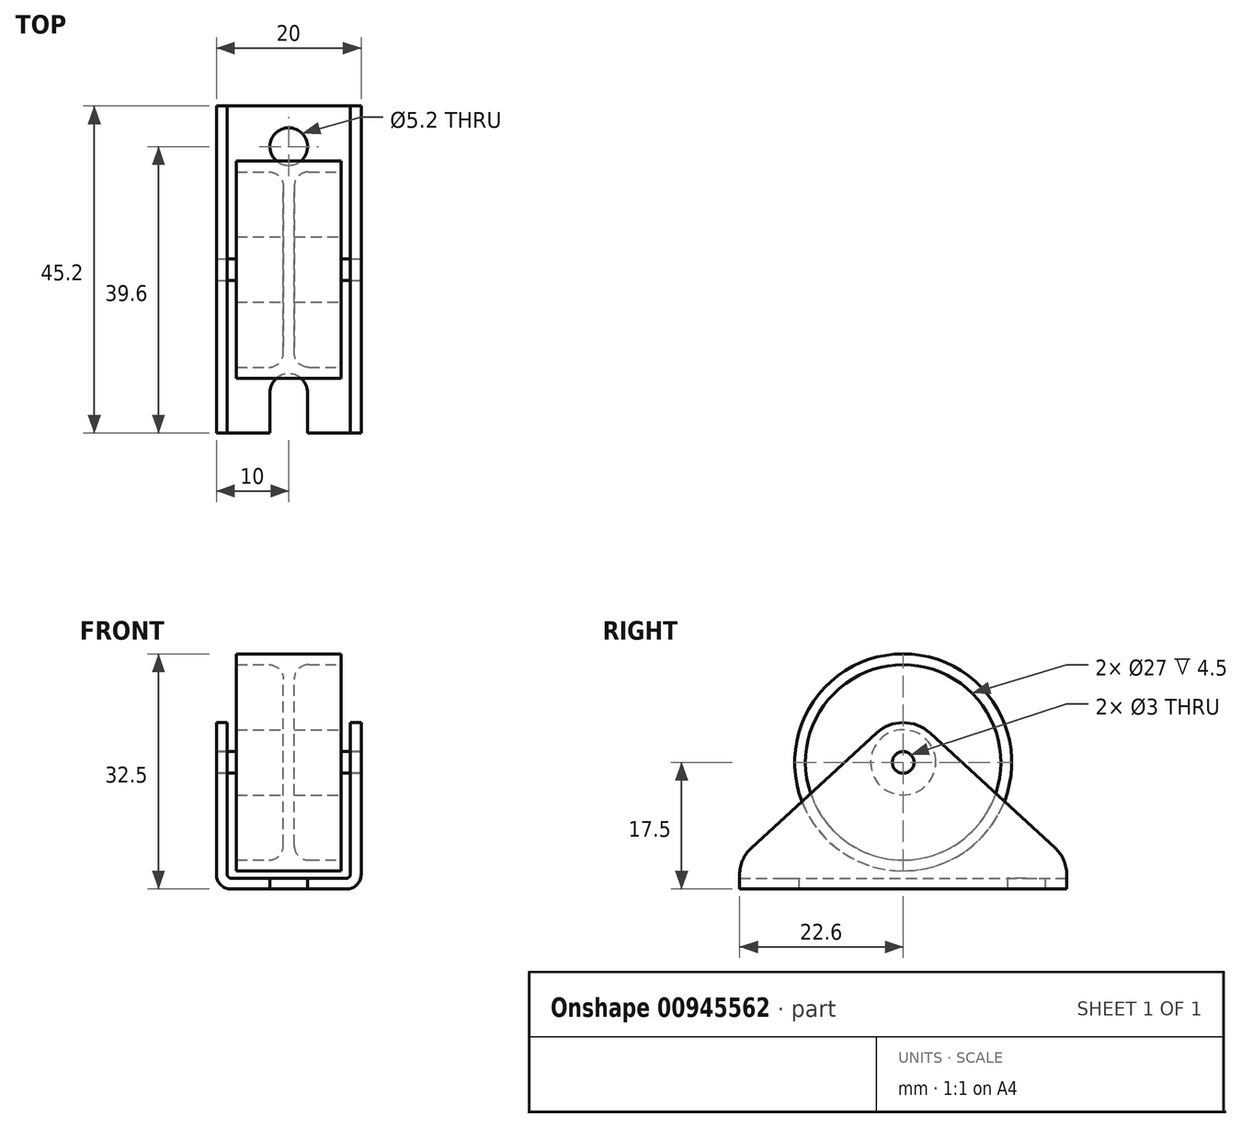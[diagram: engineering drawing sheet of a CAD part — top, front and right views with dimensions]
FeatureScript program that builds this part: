
annotation { "Feature Type Name" : "Feature", "Feature Type Description" : "" }
export const myFeature = defineFeature(function(context is Context, id is Id, definition is map)
    precondition{}
    {
        {
            var Q0;
            Q0=qCreatedBy(makeId("Front.planeOp"),FACE);
            var sketch = newSketch(context, id + "F0", { "sketchPlane" : qUnion([Q0])});
            skLineSegment(sketch, "E0.bottom", {"start": v(-8, 0) * mm, "end": v(8, 0) * mm});
            skLineSegment(sketch, "E0.top", {"start": v(-10, 23) * mm, "end": v(-8.5, 23) * mm});
            skLineSegment(sketch, "E0.left", {"start": v(-10, 2) * mm, "end": v(-10, 23) * mm});
            skLineSegment(sketch, "E0.right", {"start": v(10, 2) * mm, "end": v(10, 23) * mm});
            skLineSegment(sketch, "E1.0", {"start": v(-8.5, 2) * mm, "end": v(-8.5, 23) * mm});
            skLineSegment(sketch, "E1.1", {"start": v(-8, 1.5) * mm, "end": v(8, 1.5) * mm});
            skLineSegment(sketch, "E1.2", {"start": v(8.5, 2) * mm, "end": v(8.5, 23) * mm});
            skPoint(sketch, "E2.visualSharp", {"position": v(-8.5, 1.5) * mm});
            skArc(sketch, "E2.filletArc", {"start": v(-8.5, 2) * mm, "mid": v(-8.35, 1.65) * mm, "end": v(-8, 1.5) * mm});
            skLineSegment(sketch, "E3", {"start": v(8.5, 23) * mm, "end": v(10, 23) * mm});
            skPoint(sketch, "E4.visualSharp", {"position": v(8.5, 1.5) * mm});
            skArc(sketch, "E4.filletArc", {"start": v(8, 1.5) * mm, "mid": v(8.35, 1.65) * mm, "end": v(8.5, 2) * mm});
            skPoint(sketch, "E5.visualSharp", {"position": v(-10, 0) * mm});
            skArc(sketch, "E5.filletArc", {"start": v(-10, 2) * mm, "mid": v(-9.41, 0.59) * mm, "end": v(-8, 0) * mm});
            skPoint(sketch, "E6.visualSharp", {"position": v(10, 0) * mm});
            skArc(sketch, "E6.filletArc", {"start": v(8, 0) * mm, "mid": v(9.41, 0.59) * mm, "end": v(10, 2) * mm});
            skPoint(sketch, "E7", {"position": v(0, 0) * mm});
            skLineSegment(sketch, "E8", {"start": v(0, 0) * mm, "end": v(0, 28.77) * mm, "construction": true});
            skLineSegment(sketch, "E9", {"start": v(0, 32.5) * mm, "end": v(7.25, 32.5) * mm});
            skLineSegment(sketch, "E10", {"start": v(7.25, 32.5) * mm, "end": v(7.25, 31) * mm});
            skLineSegment(sketch, "E11", {"start": v(7.25, 31) * mm, "end": v(2.75, 31) * mm});
            skLineSegment(sketch, "E12", {"start": v(0.75, 29) * mm, "end": v(0.75, 22) * mm});
            skLineSegment(sketch, "E13", {"start": v(0.75, 22) * mm, "end": v(7.25, 22) * mm});
            skLineSegment(sketch, "E14", {"start": v(7.25, 22) * mm, "end": v(7.25, 19) * mm});
            skLineSegment(sketch, "E15", {"start": v(7.25, 19) * mm, "end": v(8.5, 19) * mm});
            skLineSegment(sketch, "E16", {"start": v(8.5, 17.5) * mm, "end": v(0, 17.5) * mm});
            skPoint(sketch, "E17.visualSharp", {"position": v(0.75, 31) * mm});
            skArc(sketch, "E17.filletArc", {"start": v(2.75, 31) * mm, "mid": v(1.34, 30.41) * mm, "end": v(0.75, 29) * mm});
            skLineSegment(sketch, "E18", {"start": v(7.25, 22) * mm, "end": v(7.25, 31) * mm, "construction": true});
            skLineSegment(sketch, "E19.0.MirrorCS", {"start": v(-8.5, 17.5) * mm, "end": v(0, 17.5) * mm});
            skLineSegment(sketch, "E20.0.MirrorCS", {"start": v(-7.25, 19) * mm, "end": v(-8.5, 19) * mm});
            skLineSegment(sketch, "E21.0.MirrorCS", {"start": v(-7.25, 22) * mm, "end": v(-7.25, 19) * mm});
            skLineSegment(sketch, "E22.0.MirrorCS", {"start": v(-0.75, 22) * mm, "end": v(-7.25, 22) * mm});
            skLineSegment(sketch, "E23.0.MirrorCS", {"start": v(-0.75, 29) * mm, "end": v(-0.75, 22) * mm});
            skArc(sketch, "E24.0.MirrorCS", {"start": v(-2.75, 31) * mm, "mid": v(-1.34, 30.41) * mm, "end": v(-0.75, 29) * mm});
            skLineSegment(sketch, "E25.0.MirrorCS", {"start": v(-7.25, 31) * mm, "end": v(-2.75, 31) * mm});
            skLineSegment(sketch, "E26.0.MirrorCS", {"start": v(-7.25, 32.5) * mm, "end": v(-7.25, 31) * mm});
            skLineSegment(sketch, "E27.0.MirrorCS", {"start": v(0, 32.5) * mm, "end": v(-7.25, 32.5) * mm});
            skLineSegment(sketch, "E28", {"start": v(8.5, 23) * mm, "end": v(-8.5, 23) * mm, "construction": true});
            skLineSegment(sketch, "E29.bottom", {"start": v(-8.5, 17.5) * mm, "end": v(-10, 17.5) * mm});
            skLineSegment(sketch, "E29.top", {"start": v(-8.5, 19) * mm, "end": v(-10, 19) * mm});
            skLineSegment(sketch, "E29.right", {"start": v(-10, 17.5) * mm, "end": v(-10, 19) * mm});
            skLineSegment(sketch, "E30.0.MirrorCS", {"start": v(8.5, 19) * mm, "end": v(10, 19) * mm});
            skLineSegment(sketch, "E31.0.MirrorCS", {"start": v(10, 17.5) * mm, "end": v(10, 19) * mm});
            skLineSegment(sketch, "E32.0.MirrorCS", {"start": v(8.5, 17.5) * mm, "end": v(10, 17.5) * mm});
            skSolve(sketch);
        }
        {
            var Q0;
            Q0=makeQuery(id+"F0.imprint","IMPRINT",FACE,{"disambiguationData":[TD([[makeQuery(id+"F0.imprint","IMPRINT",EDGE,{"derivedFrom":sQuery(id+"F0.wireOp",EDGE,"E0.bottom")}),1.0]])]});
            var Q1;
            {var subQ1=sQuery(id+"F0.wireOp",EDGE,"E29.bottom");Q1=makeQuery(id+"F0.imprint","IMPRINT",FACE,{"disambiguationData":[TD([[makeQuery(id+"F0.imprint","IMPRINT",EDGE,{"derivedFrom":subQ1}),-1.0]])]});}
            var Q2;
            {var subQ2=sQuery(id+"F0.wireOp",EDGE,"E0.top");Q2=makeQuery(id+"F0.imprint","IMPRINT",FACE,{"disambiguationData":[TD([[makeQuery(id+"F0.imprint","IMPRINT",EDGE,{"derivedFrom":subQ2}),-1.0]])]});}
            var Q3;
            {var subQ1=sQuery(id+"F0.wireOp",EDGE,"E30.0.MirrorCS");Q3=makeQuery(id+"F0.imprint","IMPRINT",FACE,{"disambiguationData":[TD([[makeQuery(id+"F0.imprint","IMPRINT",EDGE,{"derivedFrom":subQ1}),-1.0]])]});}
            var Q4;
            {var subQ0=sQuery(id+"F0.wireOp",EDGE,"E3");Q4=makeQuery(id+"F0.imprint","IMPRINT",FACE,{"disambiguationData":[TD([[makeQuery(id+"F0.imprint","IMPRINT",EDGE,{"derivedFrom":subQ0}),-1.0]])]});}
            extrude(context, id + "F1", {"entities" : qUnion([Q0, Q1, Q2, Q3, Q4]), "depth" : 22.6 * mm, "hasSecondDirection" : true, "secondDirectionOppositeDirection" : true, "secondDirectionDepth" : 22.6 * mm});
        }
        {
            var Q0;
            Q0=makeQuery(id+"F1.opExtrude","SWEPT_FACE",FACE,{"disambiguationData":[OSD([sQuery(id+"F0.wireOp",EDGE,"E0.left")])]});
            var sketch = newSketch(context, id + "F2", { "sketchPlane" : qUnion([Q0])});
            skLineSegment(sketch, "E33", {"start": v(0, 23) * mm, "end": v(0, 23) * mm});
            skLineSegment(sketch, "E34", {"start": v(3.72, 21.55) * mm, "end": v(20.98, 5.68) * mm});
            skLineSegment(sketch, "E35", {"start": v(22.6, 2) * mm, "end": v(22.6, 2) * mm});
            skPoint(sketch, "E36.visualSharp", {"position": v(2.14, 23) * mm});
            skArc(sketch, "E36.filletArc", {"start": v(3.72, 21.55) * mm, "mid": v(2, 22.62) * mm, "end": v(0, 23) * mm});
            skPoint(sketch, "E37.visualSharp", {"position": v(22.6, 4.2) * mm});
            skArc(sketch, "E37.filletArc", {"start": v(22.6, 2) * mm, "mid": v(22.18, 4.01) * mm, "end": v(20.98, 5.68) * mm});
            skLineSegment(sketch, "E38", {"start": v(0, 23) * mm, "end": v(22.6, 23) * mm});
            skLineSegment(sketch, "E39", {"start": v(22.6, 23) * mm, "end": v(22.6, 2) * mm});
            skLineSegment(sketch, "E40.0.MirrorCS", {"start": v(-22.6, 2) * mm, "end": v(-22.6, 2) * mm});
            skPoint(sketch, "E40.1.MirrorP", {"position": v(-22.6, 4.2) * mm});
            skPoint(sketch, "E40.2.MirrorP", {"position": v(-2.14, 23) * mm});
            skLineSegment(sketch, "E40.3.MirrorCS", {"start": v(0, 23) * mm, "end": v(-22.6, 23) * mm});
            skArc(sketch, "E40.4.MirrorCS", {"start": v(-22.6, 2) * mm, "mid": v(-22.18, 4.01) * mm, "end": v(-20.98, 5.68) * mm});
            skLineSegment(sketch, "E40.5.MirrorCS", {"start": v(-3.72, 21.55) * mm, "end": v(-20.98, 5.68) * mm});
            skArc(sketch, "E40.6.MirrorCS", {"start": v(-3.72, 21.55) * mm, "mid": v(-2, 22.62) * mm, "end": v(0, 23) * mm});
            skLineSegment(sketch, "E40.7.MirrorCS", {"start": v(-22.6, 23) * mm, "end": v(-22.6, 2) * mm});
            skCircle(sketch, "E41", {"center": v(0, 17.5) * mm, "radius": 1.5 * mm});
            skSolve(sketch);
        }
        {
            var Q0;
            Q0=qSketchRegion(id+"F2",true);
            extrude(context, id + "F3", {"entities" : qUnion([Q0]), "operationType" : NewBodyOperationType.REMOVE, "oppositeDirection" : true, "depth" : 25 * mm});
        }
        {
            var Q0;
            Q0=makeQuery(id+"F1.opExtrude","SWEPT_FACE",FACE,{"disambiguationData":[OSD([sQuery(id+"F0.wireOp",EDGE,"E0.bottom")])]});
            var sketch = newSketch(context, id + "F4", { "sketchPlane" : qUnion([Q0])});
            skLineSegment(sketch, "E42", {"start": v(-8, 0) * mm, "end": v(8, 0) * mm, "construction": true});
            skCircle(sketch, "E43", {"center": v(0, 17) * mm, "radius": 2.6 * mm});
            skLineSegment(sketch, "E44", {"start": v(0, 17) * mm, "end": v(0, 0) * mm, "construction": true});
            skCircle(sketch, "E45.0.MirrorC", {"center": v(0, -17) * mm, "radius": 2.6 * mm});
            skLineSegment(sketch, "E46", {"start": v(-2.6, 17) * mm, "end": v(-2.6, 22.6) * mm});
            skLineSegment(sketch, "E47", {"start": v(2.6, 17) * mm, "end": v(2.6, 22.6) * mm});
            skLineSegment(sketch, "E48", {"start": v(-2.6, 22.6) * mm, "end": v(2.6, 22.6) * mm});
            skSolve(sketch);
        }
        {
            var Q0;
            Q0=qSketchRegion(id+"F4",true);
            extrude(context, id + "F5", {"entities" : qUnion([Q0]), "operationType" : NewBodyOperationType.REMOVE, "oppositeDirection" : true, "depth" : 25 * mm});
        }
        {
            var Q0;
            Q0=makeQuery(id+"F0.imprint","IMPRINT",FACE,{"disambiguationData":[TD([[makeQuery(id+"F0.imprint","IMPRINT",EDGE,{"derivedFrom":sQuery(id+"F0.wireOp",EDGE,"E9")}),-1.0]])]});
            var Q1;
            {var subQ1=sQuery(id+"F0.wireOp",EDGE,"E30.0.MirrorCS");Q1=makeQuery(id+"F0.imprint","IMPRINT",FACE,{"disambiguationData":[TD([[makeQuery(id+"F0.imprint","IMPRINT",EDGE,{"derivedFrom":subQ1}),-1.0]])]});}
            var Q2;
            {var subQ1=sQuery(id+"F0.wireOp",EDGE,"E29.bottom");Q2=makeQuery(id+"F0.imprint","IMPRINT",FACE,{"disambiguationData":[TD([[makeQuery(id+"F0.imprint","IMPRINT",EDGE,{"derivedFrom":subQ1}),-1.0]])]});}
            var Q3;
            Q3=sQuery(id+"F0.wireOp",EDGE,"E16");
            revolve(context, id + "F6", {"entities" : qUnion([Q0, Q1, Q2]), "axis" : qUnion([Q3]), "revolveType" : RevolveType.FULL});
        }
    });
